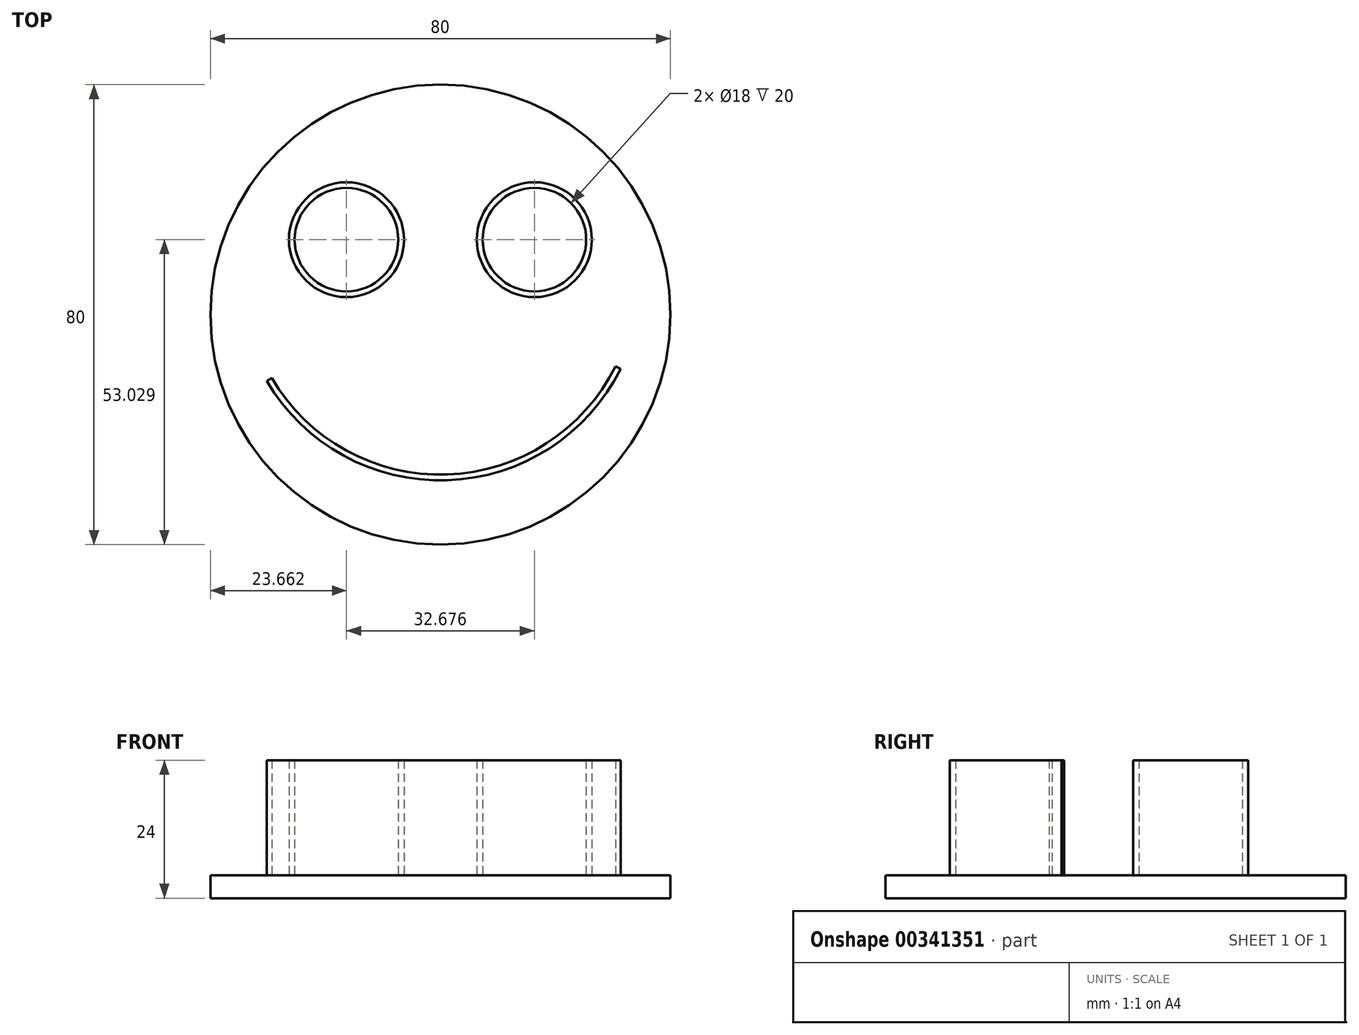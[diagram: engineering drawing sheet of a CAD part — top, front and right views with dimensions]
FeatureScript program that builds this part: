
annotation { "Feature Type Name" : "Feature", "Feature Type Description" : "" }
export const myFeature = defineFeature(function(context is Context, id is Id, definition is map)
    precondition{}
    {
        {
            var Q0;
            Q0=qCreatedBy(makeId("Top.planeOp"),FACE);
            var sketch = newSketch(context, id + "F0", { "sketchPlane" : qUnion([Q0])});
            skCircle(sketch, "E0", {"center": v(0, 0) * mm, "radius": 40 * mm});
            skSolve(sketch);
        }
        {
            var Q0;
            Q0=makeQuery(id+"F0.imprint","IMPRINT",FACE,{"disambiguationData":[TD([[makeQuery(id+"F0.imprint","IMPRINT",EDGE,{"derivedFrom":sQuery(id+"F0.wireOp",EDGE,"E0")}),1.0]])]});
            extrude(context, id + "F1", {"entities" : qUnion([Q0]), "depth" : 4 * mm});
        }
        {
            var Q0;
            Q0=makeQuery(id+"F1.opExtrude","CAP_FACE",FACE,{"disambiguationData":[OSD([sQuery(id+"F0.wireOp",EDGE,"E0")])],"isStart":false});
            var sketch = newSketch(context, id + "F2", { "sketchPlane" : qUnion([Q0])});
            skArc(sketch, "E1", {"start": v(-30.2, -11.54) * mm, "mid": v(1.2, -28.82) * mm, "end": v(31.34, -9.43) * mm});
            skArc(sketch, "E2.0", {"start": v(-29.33, -11.04) * mm, "mid": v(1.17, -27.82) * mm, "end": v(30.44, -8.98) * mm});
            skLineSegment(sketch, "E3", {"start": v(-30.2, -11.54) * mm, "end": v(-29.33, -11.04) * mm});
            skLineSegment(sketch, "E4", {"start": v(31.34, -9.43) * mm, "end": v(30.44, -8.98) * mm});
            skSolve(sketch);
        }
        {
            var Q0;
            Q0=makeQuery(id+"F2.imprint","IMPRINT",FACE,{"disambiguationData":[TD([[makeQuery(id+"F2.imprint","IMPRINT",EDGE,{"derivedFrom":sQuery(id+"F2.wireOp",EDGE,"E1")}),1.0]])]});
            var Q1;
            Q1=sQuery(id+"F2.wireOp",EDGE,"E1");
            var Q2;
            Q2=sQuery(id+"F2.wireOp",EDGE,"E2.0");
            extrude(context, id + "F3", {"entities" : qUnion([Q0]), "operationType" : NewBodyOperationType.ADD, "surfaceEntities" : qUnion([Q1, Q2]), "depth" : 20 * mm});
        }
        {
            var Q0;
            Q0=makeQuery(id+"F1.opExtrude","CAP_FACE",FACE,{"disambiguationData":[OSD([sQuery(id+"F0.wireOp",EDGE,"E0")])],"isStart":false});
            var sketch = newSketch(context, id + "F4", { "sketchPlane" : qUnion([Q0])});
            skCircle(sketch, "E5", {"center": v(16.34, 13.03) * mm, "radius": 10 * mm});
            skCircle(sketch, "E6.0", {"center": v(16.34, 13.03) * mm, "radius": 9 * mm});
            skSolve(sketch);
        }
        {
            var Q0;
            Q0=makeQuery(id+"F4.imprint","IMPRINT",FACE,{"disambiguationData":[TD([[makeQuery(id+"F4.imprint","IMPRINT",EDGE,{"derivedFrom":sQuery(id+"F4.wireOp",EDGE,"E5")}),1.0]])]});
            var Q1;
            Q1=sQuery(id+"F4.wireOp",EDGE,"E5");
            var Q2;
            Q2=sQuery(id+"F4.wireOp",EDGE,"E6.0");
            extrude(context, id + "F5", {"entities" : qUnion([Q0]), "surfaceEntities" : qUnion([Q1, Q2]), "depth" : 20 * mm});
        }
        {
            var Q0;
            Q0=makeQuery(id+"F5.opExtrude","SWEPT_BODY",BODY,{"disambiguationData":[OSD([sQuery(id+"F4.wireOp",EDGE,"E5"),sQuery(id+"F4.wireOp",EDGE,"E6.0")])]});
            var Q1;
            Q1=qCreatedBy(makeId("Right.planeOp"),FACE);
            mirror(context, id + "F6", {"operationType" : NewBodyOperationType.ADD, "entities" : qUnion([Q0]), "mirrorPlane" : qUnion([Q1])});
        }
    });
